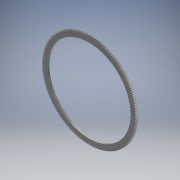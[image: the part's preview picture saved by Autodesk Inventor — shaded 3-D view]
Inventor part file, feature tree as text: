
AUTODESK INVENTOR PART (.ipt)
format: ipt  version: 2017 (Build 210142000, 142)  size: 858,624 bytes
history: native  units: mm (DEFAULTED — no unit token found)
features: plane x3, other x3, sketch x3, extrude x2
ambient origin geometry x8: Origin, YZ Plane, XZ Plane, XY Plane, X Axis, Y Axis, Z Axis, Center Point
bodies: Solid1 (feature_tree)
feature tree (11):
  extrude  "Extrusion1"  Depth=6.35mm TaperAngle=0.0deg
  plane  "Work Plane1"
  plane  "Work Plane2"
  plane  "Work Plane3"
  other  "Spur Gear"
  extrude  "Extrusion2"  Depth=76.2mm TaperAngle=0.0deg
  sketch  "Sketch1"  dims[d0=301.413333mm d1=6.35mm d2=0.0mm]
  sketch  "Sketch2"  dims[d3=298.026667mm d4=76.2mm d5=0.0mm]
  other  "Srf1"
  sketch  "Sketch3"  dims[d6=0.0mm d7=0.1785mm d9=0.0mm d14=0.0mm d15=161.713333mm d16=0.0mm d17=0.0mm d18=0.0mm d19=161.713333mm d20=266.421792mm d21=25.4mm d22=0.0mm]
  other  "Pitch Diameter"
